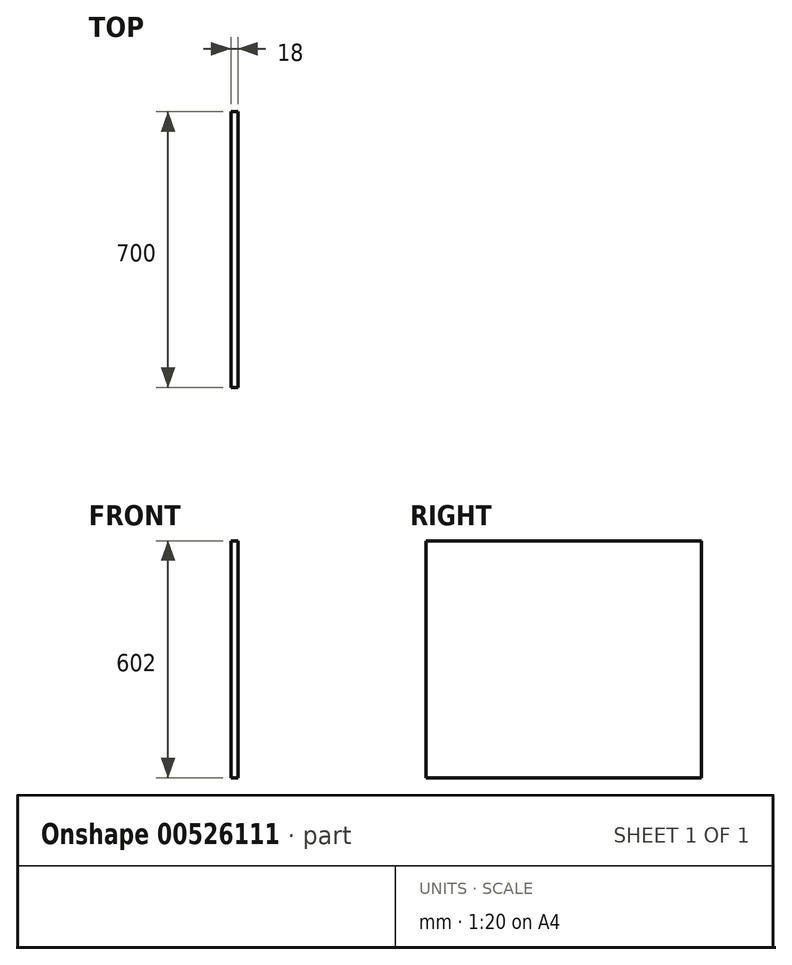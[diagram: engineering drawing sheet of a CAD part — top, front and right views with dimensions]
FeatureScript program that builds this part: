
annotation { "Feature Type Name" : "Feature", "Feature Type Description" : "" }
export const myFeature = defineFeature(function(context is Context, id is Id, definition is map)
    precondition{}
    {
        {
            var Q0;
            Q0=qCreatedBy(makeId("Right.planeOp"),FACE);
            var sketch = newSketch(context, id + "F0", { "sketchPlane" : qUnion([Q0])});
            skLineSegment(sketch, "E0.left", {"start": v(350, -310) * mm, "end": v(350, 292) * mm});
            skLineSegment(sketch, "E1.left", {"start": v(350, 162) * mm, "end": v(350, 292) * mm});
            skLineSegment(sketch, "E1.right", {"start": v(-350, 162) * mm, "end": v(-350, 292) * mm});
            skLineSegment(sketch, "E2.bottom", {"start": v(350, -310) * mm, "end": v(-350, -310) * mm});
            skLineSegment(sketch, "E2.top", {"start": v(350, 292) * mm, "end": v(-350, 292) * mm});
            skLineSegment(sketch, "E2.right", {"start": v(-350, -310) * mm, "end": v(-350, 292) * mm});
            skPoint(sketch, "E2.middle", {"position": v(0, -9) * mm});
            skSolve(sketch);
        }
        {
            var Q0;
            Q0=qSketchRegion(id+"F0",true);
            extrude(context, id + "F1", {"entities" : qUnion([Q0]), "depth" : 9 * mm});
        }
        {
            var Q0;
            Q0 = qSketchRegion(id + "F0", true);
            extrude(context, id + "F2", {"entities" : qUnion([Q0]), "operationType" : NewBodyOperationType.ADD, "depth" : 18 * mm, "offsetDistance" : 25 * mm});
        }
    });
